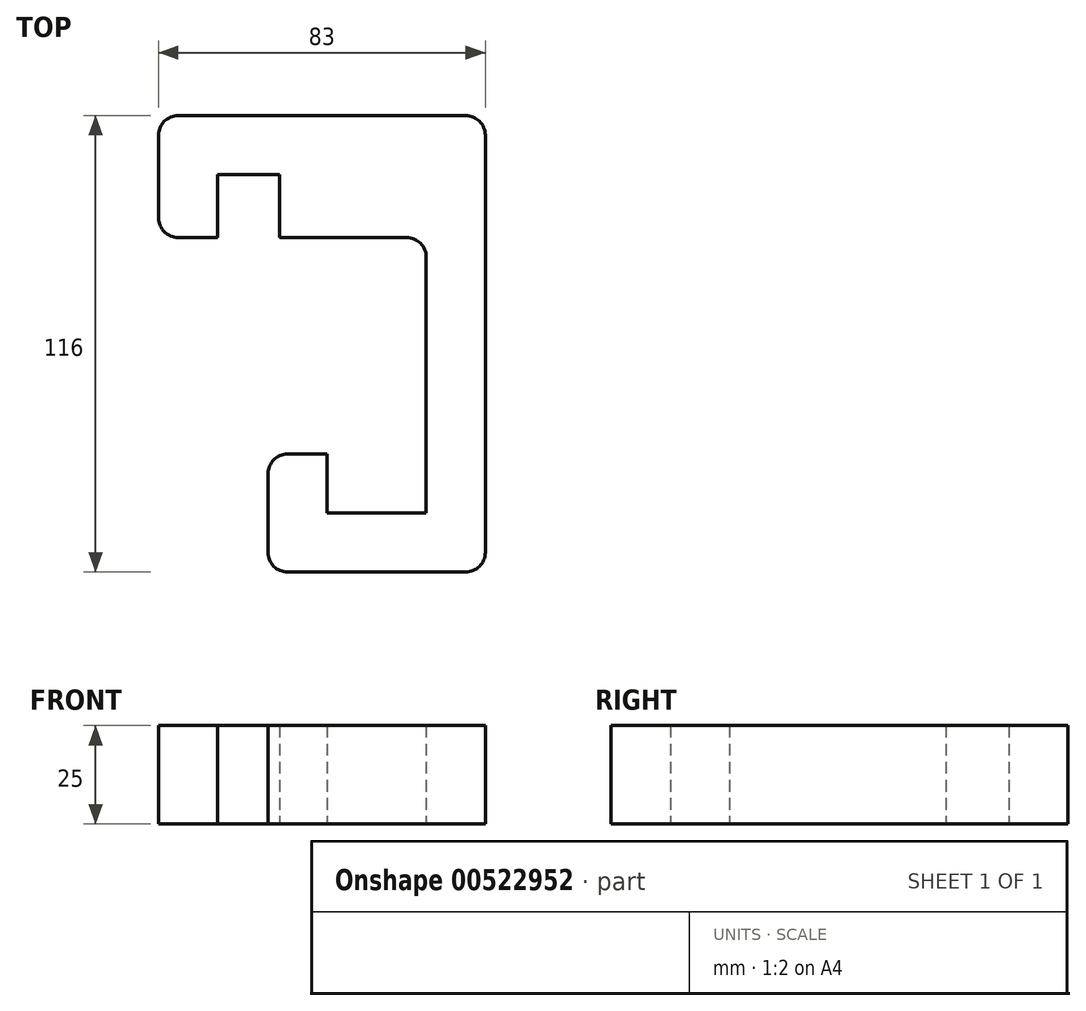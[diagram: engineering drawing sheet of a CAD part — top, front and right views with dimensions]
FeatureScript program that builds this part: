
annotation { "Feature Type Name" : "Feature", "Feature Type Description" : "" }
export const myFeature = defineFeature(function(context is Context, id is Id, definition is map)
    precondition{}
    {
        {
            var Q0;
            Q0=qCreatedBy(makeId("Top.planeOp"),FACE);
            var sketch = newSketch(context, id + "F0", { "sketchPlane" : qUnion([Q0])});
            skLineSegment(sketch, "E0", {"start": v(-53, 35) * mm, "end": v(-63, 35) * mm});
            skLineSegment(sketch, "E1", {"start": v(-68, 40) * mm, "end": v(-68, 61) * mm});
            skLineSegment(sketch, "E2", {"start": v(-63, 66) * mm, "end": v(10, 66) * mm});
            skLineSegment(sketch, "E3", {"start": v(15, 61) * mm, "end": v(15, -45) * mm});
            skLineSegment(sketch, "E4", {"start": v(10, -50) * mm, "end": v(-35.2, -50) * mm});
            skLineSegment(sketch, "E5", {"start": v(-40.2, -45) * mm, "end": v(-40.2, -25) * mm});
            skLineSegment(sketch, "E6", {"start": v(-35.2, -20) * mm, "end": v(-25.2, -20) * mm});
            skLineSegment(sketch, "E7", {"start": v(-25.2, -20) * mm, "end": v(-25.2, -35) * mm});
            skLineSegment(sketch, "E8", {"start": v(-25.2, -35) * mm, "end": v(0, -35) * mm});
            skLineSegment(sketch, "E9", {"start": v(0, -35) * mm, "end": v(0, 30) * mm});
            skLineSegment(sketch, "E10", {"start": v(-5, 35) * mm, "end": v(-37.2, 35) * mm});
            skLineSegment(sketch, "E11", {"start": v(-37.2, 35) * mm, "end": v(-37.2, 51) * mm});
            skLineSegment(sketch, "E12", {"start": v(-37.2, 51) * mm, "end": v(-53, 51) * mm});
            skLineSegment(sketch, "E13", {"start": v(-53, 51) * mm, "end": v(-53, 35) * mm});
            skPoint(sketch, "E14", {"position": v(0, 0) * mm});
            skPoint(sketch, "E15.visualSharp", {"position": v(-68, 66) * mm});
            skArc(sketch, "E15.filletArc", {"start": v(-63, 66) * mm, "mid": v(-66.54, 64.54) * mm, "end": v(-68, 61) * mm});
            skPoint(sketch, "E16.visualSharp", {"position": v(15, 66) * mm});
            skArc(sketch, "E16.filletArc", {"start": v(15, 61) * mm, "mid": v(13.54, 64.54) * mm, "end": v(10, 66) * mm});
            skPoint(sketch, "E17.visualSharp", {"position": v(0, 35) * mm});
            skArc(sketch, "E17.filletArc", {"start": v(0, 30) * mm, "mid": v(-1.46, 33.54) * mm, "end": v(-5, 35) * mm});
            skPoint(sketch, "E18.visualSharp", {"position": v(-68, 35) * mm});
            skArc(sketch, "E18.filletArc", {"start": v(-68, 40) * mm, "mid": v(-66.54, 36.46) * mm, "end": v(-63, 35) * mm});
            skPoint(sketch, "E19.visualSharp", {"position": v(-40.2, -20) * mm});
            skArc(sketch, "E19.filletArc", {"start": v(-35.2, -20) * mm, "mid": v(-38.74, -21.46) * mm, "end": v(-40.2, -25) * mm});
            skPoint(sketch, "E20.visualSharp", {"position": v(-40.2, -50) * mm});
            skArc(sketch, "E20.filletArc", {"start": v(-40.2, -45) * mm, "mid": v(-38.74, -48.54) * mm, "end": v(-35.2, -50) * mm});
            skPoint(sketch, "E21.visualSharp", {"position": v(15, -50) * mm});
            skArc(sketch, "E21.filletArc", {"start": v(10, -50) * mm, "mid": v(13.54, -48.54) * mm, "end": v(15, -45) * mm});
            skSolve(sketch);
        }
        {
            var Q0;
            Q0 = qSketchRegion(id + "F0", true);
            extrude(context, id + "F1", {"entities" : qUnion([Q0]), "depth" : 25 * mm, "offsetDistance" : 25 * mm});
        }
    });
